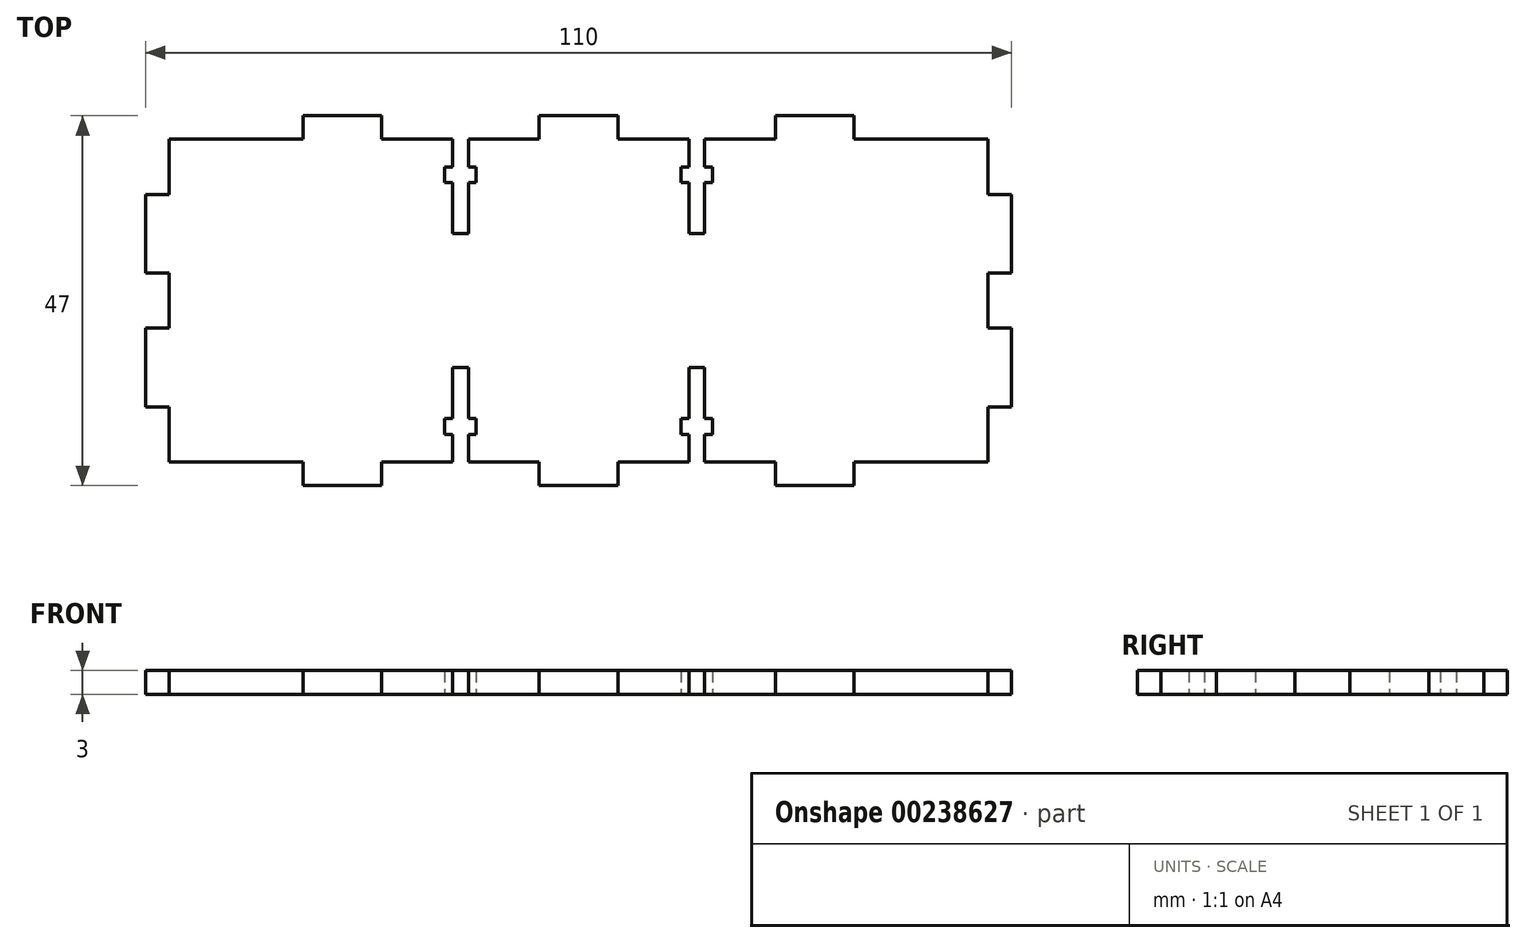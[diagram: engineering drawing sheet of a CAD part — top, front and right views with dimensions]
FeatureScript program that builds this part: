
annotation { "Feature Type Name" : "Feature", "Feature Type Description" : "" }
export const myFeature = defineFeature(function(context is Context, id is Id, definition is map)
    precondition{}
    {
        {
            var Q0;
            Q0=qCreatedBy(makeId("Top.planeOp"),FACE);
            var sketch = newSketch(context, id + "F0", { "sketchPlane" : qUnion([Q0])});
            skLineSegment(sketch, "E0.bottom", {"start": v(52, 20.5) * mm, "end": v(35, 20.5) * mm});
            skLineSegment(sketch, "E0.top", {"start": v(52, -20.5) * mm, "end": v(35, -20.5) * mm});
            skLineSegment(sketch, "E0.left", {"start": v(52, 20.5) * mm, "end": v(52, 13.5) * mm});
            skLineSegment(sketch, "E0.right", {"start": v(-52, 20.5) * mm, "end": v(-52, 13.5) * mm});
            skPoint(sketch, "E0.middle", {"position": v(0, 0) * mm});
            skLineSegment(sketch, "E1.bottom", {"start": v(-52, 13.5) * mm, "end": v(-55, 13.5) * mm});
            skLineSegment(sketch, "E1.top", {"start": v(-52, 3.5) * mm, "end": v(-55, 3.5) * mm});
            skLineSegment(sketch, "E1.right", {"start": v(-55, 13.5) * mm, "end": v(-55, 3.5) * mm});
            skLineSegment(sketch, "E2.bottom", {"start": v(-52, -3.5) * mm, "end": v(-55, -3.5) * mm});
            skLineSegment(sketch, "E2.top", {"start": v(-52, -13.5) * mm, "end": v(-55, -13.5) * mm});
            skLineSegment(sketch, "E2.right", {"start": v(-55, -3.5) * mm, "end": v(-55, -13.5) * mm});
            skLineSegment(sketch, "E3.top", {"start": v(-35, 23.5) * mm, "end": v(-25, 23.5) * mm});
            skLineSegment(sketch, "E3.left", {"start": v(-35, 20.5) * mm, "end": v(-35, 23.5) * mm});
            skLineSegment(sketch, "E3.right", {"start": v(-25, 20.5) * mm, "end": v(-25, 23.5) * mm});
            skLineSegment(sketch, "E4.MirrorCS", {"start": v(-35, -23.5) * mm, "end": v(-25, -23.5) * mm});
            skLineSegment(sketch, "E5.MirrorCS", {"start": v(-35, -20.5) * mm, "end": v(-35, -23.5) * mm});
            skLineSegment(sketch, "E6.MirrorCS", {"start": v(-25, -20.5) * mm, "end": v(-25, -23.5) * mm});
            skLineSegment(sketch, "E7.top", {"start": v(-16, 8.5) * mm, "end": v(-14, 8.5) * mm});
            skLineSegment(sketch, "E7.left", {"start": v(-16, 20.5) * mm, "end": v(-16, 17) * mm});
            skLineSegment(sketch, "E8.bottom", {"start": v(-17, 17) * mm, "end": v(-16, 17) * mm});
            skLineSegment(sketch, "E8.top", {"start": v(-17, 15) * mm, "end": v(-16, 15) * mm});
            skLineSegment(sketch, "E8.left", {"start": v(-17, 17) * mm, "end": v(-17, 15) * mm});
            skLineSegment(sketch, "E8.right", {"start": v(-13, 17) * mm, "end": v(-13, 15) * mm});
            skLineSegment(sketch, "E9.MirrorCS", {"start": v(-16, -8.5) * mm, "end": v(-14, -8.5) * mm});
            skLineSegment(sketch, "E10.MirrorCS", {"start": v(-14, -20.5) * mm, "end": v(-14, -17) * mm});
            skLineSegment(sketch, "E11.MirrorCS", {"start": v(-16, -20.5) * mm, "end": v(-16, -17) * mm});
            skLineSegment(sketch, "E12.MirrorCS", {"start": v(14, 20.5) * mm, "end": v(14, 17) * mm});
            skLineSegment(sketch, "E13.MirrorCS", {"start": v(17, 17) * mm, "end": v(16, 17) * mm});
            skLineSegment(sketch, "E14.MirrorCS", {"start": v(13, 17) * mm, "end": v(13, 15) * mm});
            skLineSegment(sketch, "E15.MirrorCS", {"start": v(17, 17) * mm, "end": v(17, 15) * mm});
            skLineSegment(sketch, "E16.MirrorCS", {"start": v(16, 20.5) * mm, "end": v(16, 17) * mm});
            skLineSegment(sketch, "E17.MirrorCS", {"start": v(16, 8.5) * mm, "end": v(14, 8.5) * mm});
            skLineSegment(sketch, "E18.MirrorCS", {"start": v(17, 15) * mm, "end": v(16, 15) * mm});
            skLineSegment(sketch, "E19.MirrorCS", {"start": v(16, -8.5) * mm, "end": v(14, -8.5) * mm});
            skLineSegment(sketch, "E20.trimOffspring", {"start": v(-14, 17) * mm, "end": v(-13, 17) * mm});
            skLineSegment(sketch, "E21.trimOffspring", {"start": v(-14, 15) * mm, "end": v(-14, 8.5) * mm});
            skLineSegment(sketch, "E22", {"start": v(-14, 17) * mm, "end": v(-14, 20.5) * mm});
            skLineSegment(sketch, "E23.trimOffspring", {"start": v(-14, 15) * mm, "end": v(-13, 15) * mm});
            skLineSegment(sketch, "E24.trimOffspring", {"start": v(-16, 15) * mm, "end": v(-16, 8.5) * mm});
            skLineSegment(sketch, "E25.trimOffspring", {"start": v(14, 17) * mm, "end": v(13, 17) * mm});
            skLineSegment(sketch, "E26.trimOffspring", {"start": v(16, 15) * mm, "end": v(16, 8.5) * mm});
            skLineSegment(sketch, "E27.trimOffspring", {"start": v(14, 15) * mm, "end": v(13, 15) * mm});
            skLineSegment(sketch, "E28.trimOffspring", {"start": v(14, 15) * mm, "end": v(14, 8.5) * mm});
            skLineSegment(sketch, "E29", {"start": v(16, -8.5) * mm, "end": v(16, -15) * mm});
            skLineSegment(sketch, "E30.bottom", {"start": v(-17, -15) * mm, "end": v(-16, -15) * mm});
            skLineSegment(sketch, "E30.top", {"start": v(-17, -17) * mm, "end": v(-16, -17) * mm});
            skLineSegment(sketch, "E30.left", {"start": v(-17, -15) * mm, "end": v(-17, -17) * mm});
            skLineSegment(sketch, "E30.right", {"start": v(-13, -15) * mm, "end": v(-13, -17) * mm});
            skLineSegment(sketch, "E31.trimOffspring", {"start": v(-16, 20.5) * mm, "end": v(-25, 20.5) * mm});
            skLineSegment(sketch, "E32.trimOffspring", {"start": v(14, 20.5) * mm, "end": v(5, 20.5) * mm});
            skLineSegment(sketch, "E33.trimOffspring", {"start": v(14, -20.5) * mm, "end": v(5, -20.5) * mm});
            skLineSegment(sketch, "E34.trimOffspring", {"start": v(-16, -20.5) * mm, "end": v(-25, -20.5) * mm});
            skLineSegment(sketch, "E35.trimOffspring", {"start": v(-14, -15) * mm, "end": v(-13, -15) * mm});
            skLineSegment(sketch, "E36.trimOffspring", {"start": v(-14, -17) * mm, "end": v(-13, -17) * mm});
            skLineSegment(sketch, "E37.trimOffspring", {"start": v(-16, -15) * mm, "end": v(-16, -8.5) * mm});
            skLineSegment(sketch, "E38.trimOffspring", {"start": v(-14, -15) * mm, "end": v(-14, -8.5) * mm});
            skPoint(sketch, "E39.MirrorCS.start.orphan", {"position": v(-16, -20.5) * mm});
            skLineSegment(sketch, "E40.MirrorCS", {"start": v(17, -15) * mm, "end": v(16, -15) * mm});
            skLineSegment(sketch, "E41.MirrorCS", {"start": v(17, -17) * mm, "end": v(16, -17) * mm});
            skLineSegment(sketch, "E42.MirrorCS", {"start": v(16, -15) * mm, "end": v(16, -8.5) * mm});
            skLineSegment(sketch, "E43.MirrorCS", {"start": v(14, -15) * mm, "end": v(14, -8.5) * mm});
            skLineSegment(sketch, "E44.MirrorCS", {"start": v(14, -17) * mm, "end": v(13, -17) * mm});
            skLineSegment(sketch, "E45.MirrorCS", {"start": v(14, -15) * mm, "end": v(13, -15) * mm});
            skLineSegment(sketch, "E46.MirrorCS", {"start": v(17, -15) * mm, "end": v(17, -17) * mm});
            skLineSegment(sketch, "E47.MirrorCS", {"start": v(13, -15) * mm, "end": v(13, -17) * mm});
            skLineSegment(sketch, "E48.trimOffspring", {"start": v(14, -17) * mm, "end": v(14, -20.5) * mm});
            skLineSegment(sketch, "E49.trimOffspring", {"start": v(16, -17) * mm, "end": v(16, -20.5) * mm});
            skLineSegment(sketch, "E50.MirrorCS", {"start": v(35, 23.5) * mm, "end": v(25, 23.5) * mm});
            skLineSegment(sketch, "E51.MirrorCS", {"start": v(35, 20.5) * mm, "end": v(35, 23.5) * mm});
            skLineSegment(sketch, "E52.MirrorCS", {"start": v(25, 20.5) * mm, "end": v(25, 23.5) * mm});
            skLineSegment(sketch, "E53.MirrorCS", {"start": v(35, -20.5) * mm, "end": v(35, -23.5) * mm});
            skLineSegment(sketch, "E54.MirrorCS", {"start": v(25, -20.5) * mm, "end": v(25, -23.5) * mm});
            skLineSegment(sketch, "E55.MirrorCS", {"start": v(35, -23.5) * mm, "end": v(25, -23.5) * mm});
            skLineSegment(sketch, "E56.MirrorCS", {"start": v(52, 3.5) * mm, "end": v(55, 3.5) * mm});
            skLineSegment(sketch, "E57.MirrorCS", {"start": v(52, 13.5) * mm, "end": v(55, 13.5) * mm});
            skLineSegment(sketch, "E58.MirrorCS", {"start": v(52, -3.5) * mm, "end": v(55, -3.5) * mm});
            skLineSegment(sketch, "E59.MirrorCS", {"start": v(52, -13.5) * mm, "end": v(55, -13.5) * mm});
            skLineSegment(sketch, "E60.MirrorCS", {"start": v(55, 13.5) * mm, "end": v(55, 3.5) * mm});
            skLineSegment(sketch, "E61.MirrorCS", {"start": v(55, -3.5) * mm, "end": v(55, -13.5) * mm});
            skLineSegment(sketch, "E62.top", {"start": v(-5, 23.5) * mm, "end": v(5, 23.5) * mm});
            skLineSegment(sketch, "E62.left", {"start": v(-5, 20.5) * mm, "end": v(-5, 23.5) * mm});
            skLineSegment(sketch, "E62.right", {"start": v(5, 20.5) * mm, "end": v(5, 23.5) * mm});
            skLineSegment(sketch, "E63.MirrorCS", {"start": v(5, -20.5) * mm, "end": v(5, -23.5) * mm});
            skLineSegment(sketch, "E64.MirrorCS", {"start": v(-5, -23.5) * mm, "end": v(5, -23.5) * mm});
            skLineSegment(sketch, "E65.MirrorCS", {"start": v(-5, -20.5) * mm, "end": v(-5, -23.5) * mm});
            skLineSegment(sketch, "E66.trimOffspring", {"start": v(-52, 3.5) * mm, "end": v(-52, -3.5) * mm});
            skLineSegment(sketch, "E67.trimOffspring", {"start": v(-35, 20.5) * mm, "end": v(-52, 20.5) * mm});
            skLineSegment(sketch, "E68.trimOffspring", {"start": v(-35, -20.5) * mm, "end": v(-52, -20.5) * mm});
            skLineSegment(sketch, "E69.trimOffspring", {"start": v(-5, -20.5) * mm, "end": v(-14, -20.5) * mm});
            skLineSegment(sketch, "E70.trimOffspring", {"start": v(-5, 20.5) * mm, "end": v(-14, 20.5) * mm});
            skLineSegment(sketch, "E71.trimOffspring", {"start": v(25, 20.5) * mm, "end": v(16, 20.5) * mm});
            skLineSegment(sketch, "E72.trimOffspring", {"start": v(52, 3.5) * mm, "end": v(52, -3.5) * mm});
            skLineSegment(sketch, "E73.trimOffspring", {"start": v(52, -13.5) * mm, "end": v(52, -20.5) * mm});
            skLineSegment(sketch, "E74.trimOffspring", {"start": v(25, -20.5) * mm, "end": v(16, -20.5) * mm});
            skLineSegment(sketch, "E75.trimOffspring", {"start": v(-52, -13.5) * mm, "end": v(-52, -20.5) * mm});
            skSolve(sketch);
        }
        {
            var Q0;
            Q0=qSketchRegion(id+"F0",true);
            extrude(context, id + "F1", {"entities" : qUnion([Q0]), "depth" : 3 * mm});
        }
    });
